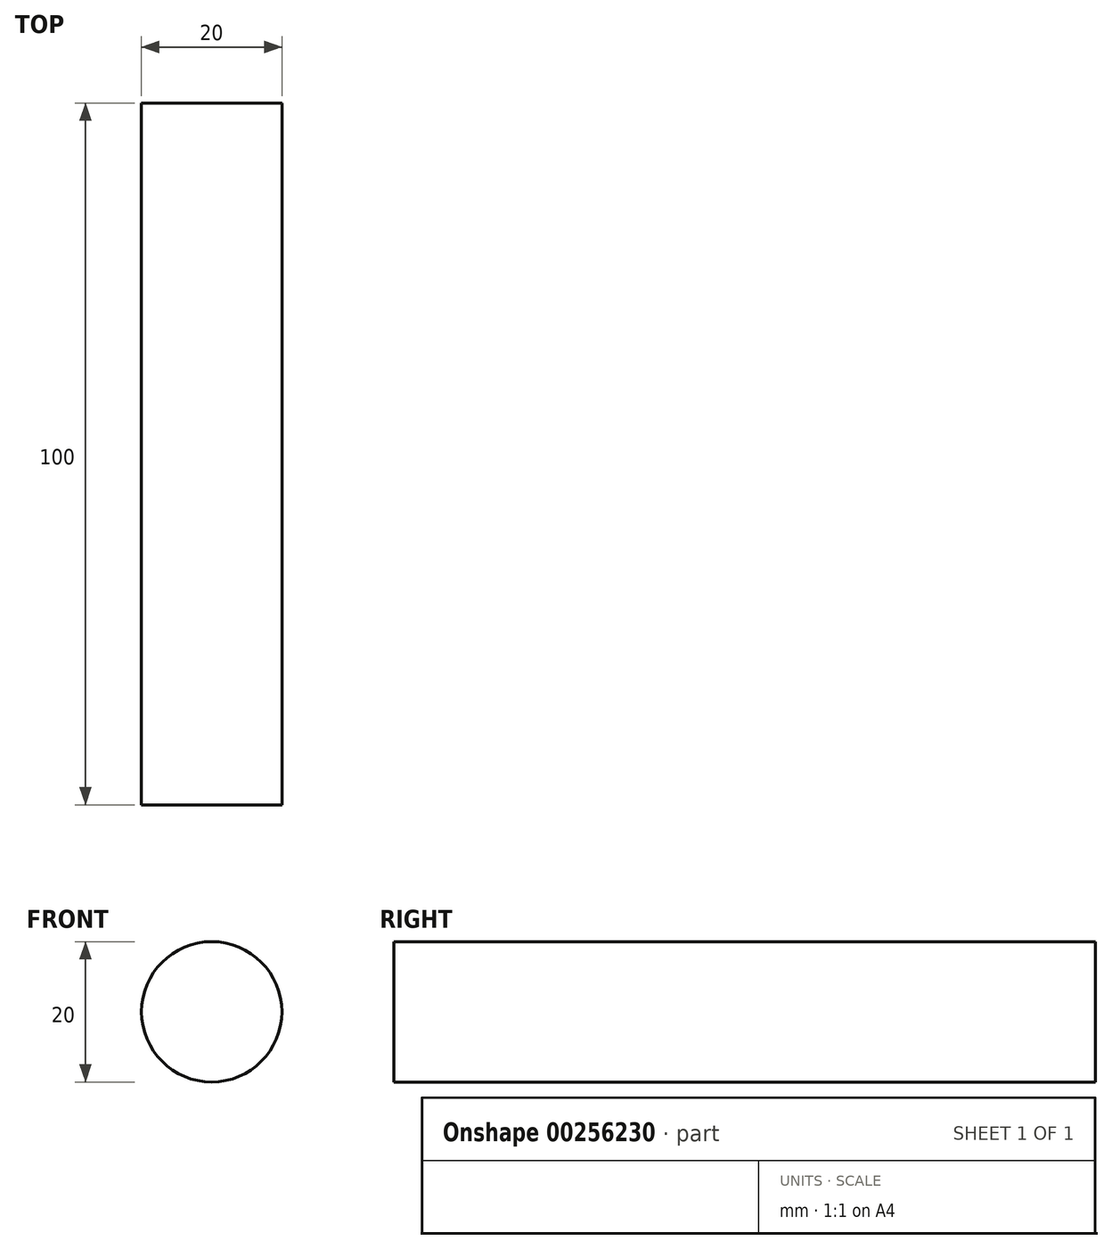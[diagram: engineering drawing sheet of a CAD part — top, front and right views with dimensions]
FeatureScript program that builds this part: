
annotation { "Feature Type Name" : "Feature", "Feature Type Description" : "" }
export const myFeature = defineFeature(function(context is Context, id is Id, definition is map)
    precondition{}
    {
        {
            var Q0;
            Q0=qCreatedBy(makeId("Front.planeOp"),FACE);
            var sketch = newSketch(context, id + "F0", { "sketchPlane" : qUnion([Q0])});
            skCircle(sketch, "E0", {"center": v(0, 0) * mm, "radius": 10 * mm});
            skSolve(sketch);
        }
        {
            var Q0;
            Q0 = qSketchRegion(id + "F0", true);
            extrude(context, id + "F1", {"entities" : qUnion([Q0]), "depth" : 100 * mm});
        }
    });
